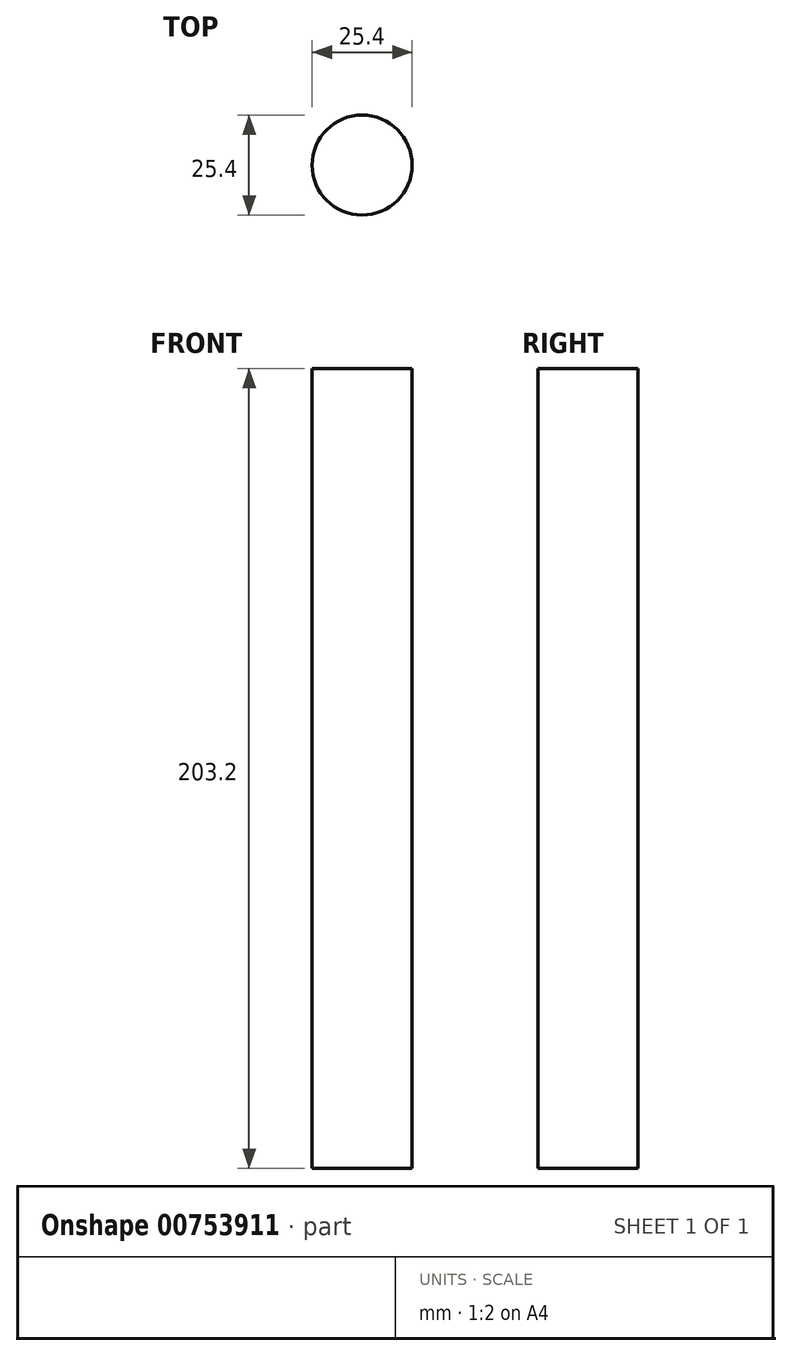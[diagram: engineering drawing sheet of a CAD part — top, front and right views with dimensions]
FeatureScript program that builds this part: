
annotation { "Feature Type Name" : "Feature", "Feature Type Description" : "" }
export const myFeature = defineFeature(function(context is Context, id is Id, definition is map)
    precondition{}
    {
        {
            var Q0;
            Q0=qCreatedBy(makeId("Top.planeOp"),FACE);
            var sketch = newSketch(context, id + "F0", { "sketchPlane" : qUnion([Q0])});
            skCircle(sketch, "E0", {"center": v(0, 0) * mm, "radius": 12.7 * mm});
            skSolve(sketch);
        }
        {
            var Q0;
            Q0 = qSketchRegion(id + "F0", true);
            var Q1;
            Q1=makeQuery(id+"F0.imprint","IMPRINT",FACE,{"disambiguationData":[TD([[makeQuery(id+"F0.imprint","IMPRINT",EDGE,{"derivedFrom":sQuery(id+"F0.wireOp",EDGE,"E0")}),1.0]])]});
            extrude(context, id + "F1", {"entities" : qUnion([Q0, Q1]), "depth" : 203.2 * mm, "offsetDistance" : 25.4 * mm});
        }
    });
